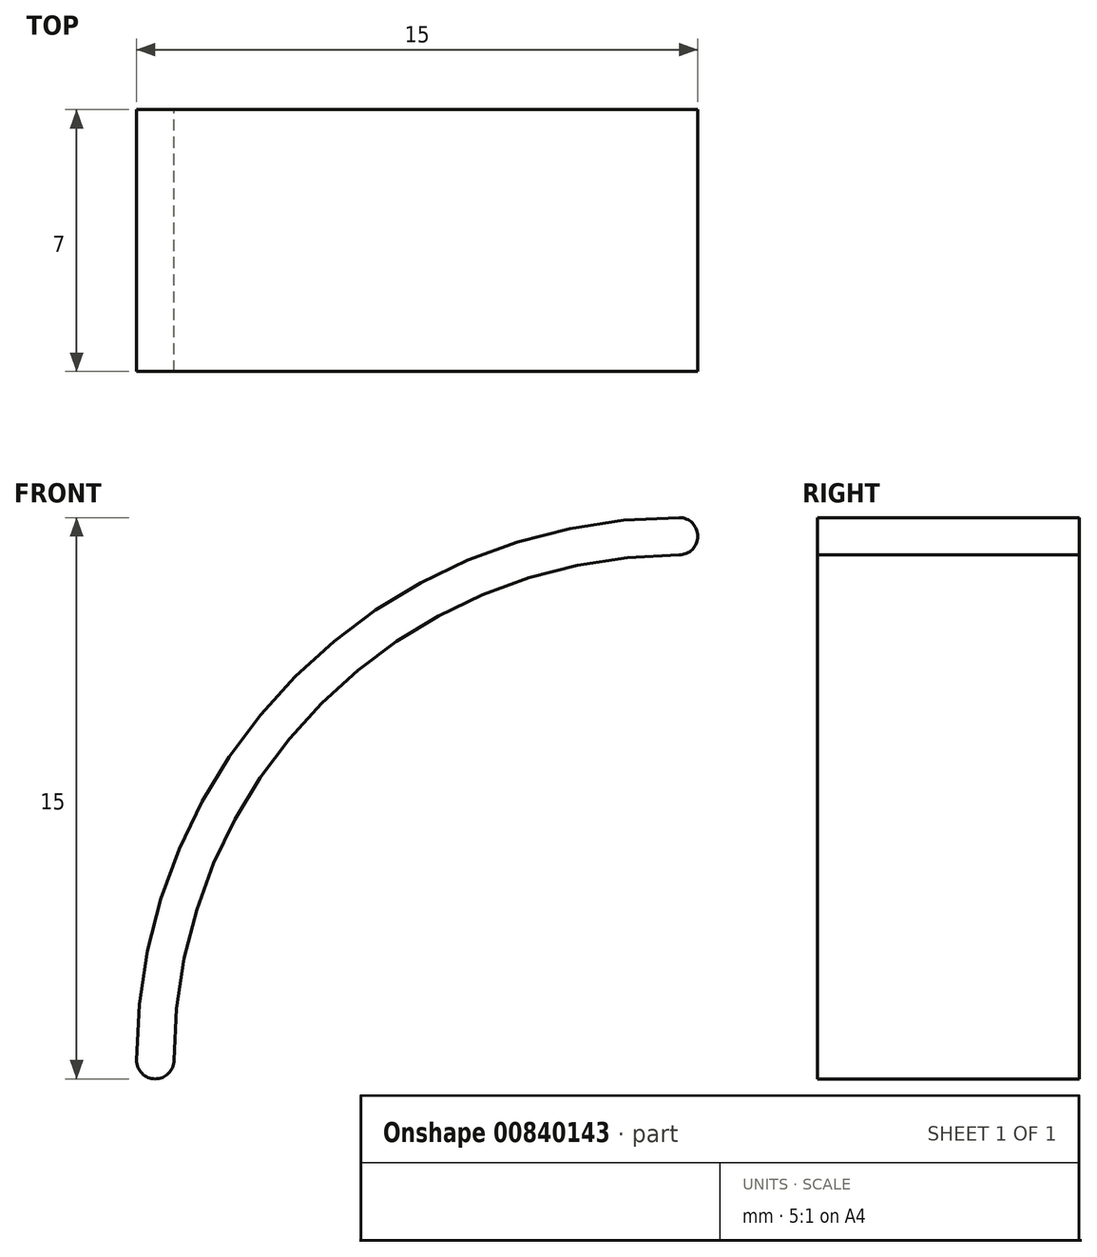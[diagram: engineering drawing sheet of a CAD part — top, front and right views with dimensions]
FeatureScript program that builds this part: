
annotation { "Feature Type Name" : "Feature", "Feature Type Description" : "" }
export const myFeature = defineFeature(function(context is Context, id is Id, definition is map)
    precondition{}
    {
        {
            var Q0;
            Q0=qCreatedBy(makeId("Front.planeOp"),FACE);
            var sketch = newSketch(context, id + "F0", { "sketchPlane" : qUnion([Q0])});
            skArc(sketch, "E0", {"start": v(0, 13.5) * mm, "mid": v(-9.55, 9.55) * mm, "end": v(-13.5, 0) * mm});
            skArc(sketch, "E1", {"start": v(0, 14.5) * mm, "mid": v(-10.25, 10.25) * mm, "end": v(-14.5, 0) * mm});
            skLineSegment(sketch, "E2", {"start": v(0, 13.5) * mm, "end": v(0, 14.5) * mm, "construction": true});
            skLineSegment(sketch, "E3", {"start": v(-13.5, 0) * mm, "end": v(-14.5, 0) * mm, "construction": true});
            skArc(sketch, "E4", {"start": v(-14.5, 0) * mm, "mid": v(-14, -0.5) * mm, "end": v(-13.5, 0) * mm});
            skArc(sketch, "E5", {"start": v(0, 13.5) * mm, "mid": v(0.5, 14) * mm, "end": v(0, 14.5) * mm});
            skSolve(sketch);
        }
        {
            var Q0;
            Q0=makeQuery(id+"F0.imprint","IMPRINT",FACE,{"disambiguationData":[TD([[makeQuery(id+"F0.imprint","IMPRINT",EDGE,{"derivedFrom":sQuery(id+"F0.wireOp",EDGE,"E0")}),-1.0]])]});
            extrude(context, id + "F1", {"entities" : qUnion([Q0]), "depth" : 7 * mm, "offsetDistance" : 25 * mm});
        }
    });
